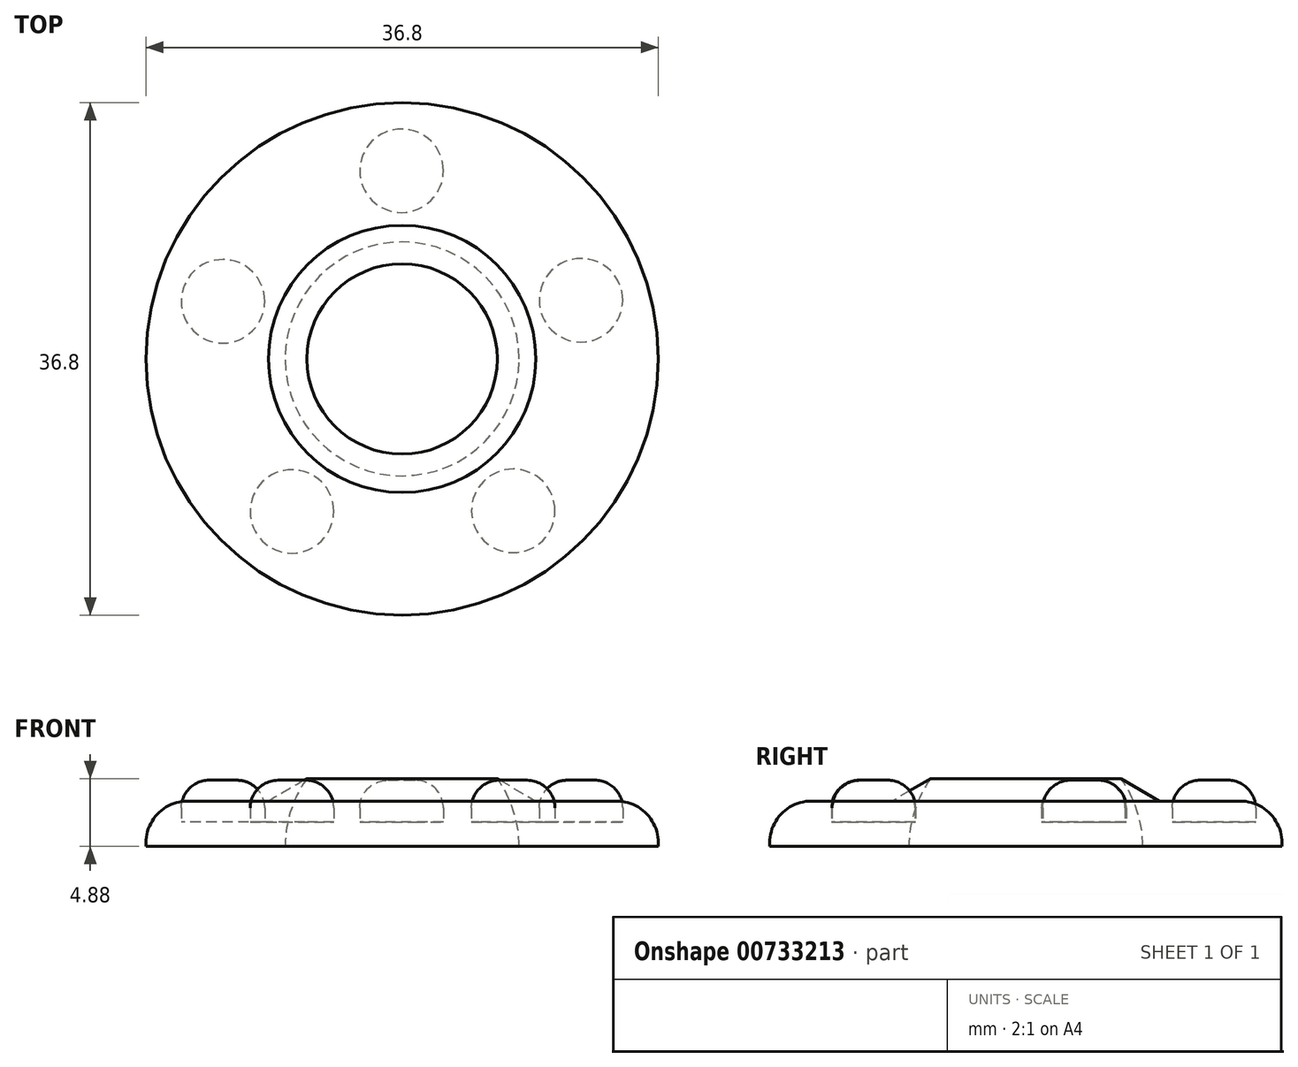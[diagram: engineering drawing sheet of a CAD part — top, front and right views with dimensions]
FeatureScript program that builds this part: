
annotation { "Feature Type Name" : "Feature", "Feature Type Description" : "" }
export const myFeature = defineFeature(function(context is Context, id is Id, definition is map)
    precondition{}
    {
        {
            var Q0;
            Q0=qCreatedBy(makeId("Front.planeOp"),FACE);
            var sketch = newSketch(context, id + "F0", { "sketchPlane" : qUnion([Q0])});
            skLineSegment(sketch, "E0", {"start": v(0, 7.97) * mm, "end": v(0, 8.4) * mm});
            skArc(sketch, "E1", {"start": v(-6.84, 4.88) * mm, "mid": v(-8, 2.56) * mm, "end": v(-8.4, 0) * mm});
            skLineSegment(sketch, "E2", {"start": v(-18.4, 0) * mm, "end": v(-18.4, 4.3) * mm});
            skLineSegment(sketch, "E3", {"start": v(-21.26, 3.26) * mm, "end": v(-9.6, 3.26) * mm});
            skLineSegment(sketch, "E4.trimOffspring", {"start": v(-8.4, 0) * mm, "end": v(-18.4, 0) * mm});
            skCircle(sketch, "E5", {"center": v(0, 0) * mm, "radius": 8 * mm});
            skLineSegment(sketch, "E6", {"start": v(0, 0) * mm, "end": v(-8, 0) * mm});
            skLineSegment(sketch, "E7", {"start": v(-9.6, 3.26) * mm, "end": v(-6.84, 4.88) * mm});
            skSolve(sketch);
        }
        {
            var Q0;
            Q0=makeQuery(id+"F0.imprint","IMPRINT",FACE,{"disambiguationData":[TD([[makeQuery(id+"F0.imprint","IMPRINT",EDGE,{"derivedFrom":sQuery(id+"F0.wireOp",EDGE,"E1")}),-1.0]])]});
            var Q1;
            Q1=sQuery(id+"F0.wireOp",EDGE,"E0");
            revolve(context, id + "F1", {"surfaceOperationType" : NewSurfaceOperationType.NEW, "entities" : qUnion([Q0]), "axis" : qUnion([Q1]), "revolveType" : RevolveType.FULL});
        }
        {
            var Q0;
            Q0=makeQuery(id+"F1.opRevolve","SWEPT_FACE",FACE,{"disambiguationData":[OSD([sQuery(id+"F0.wireOp",EDGE,"E3")])]});
            var sketch = newSketch(context, id + "F2", { "sketchPlane" : qUnion([Q0])});
            skCircle(sketch, "E8", {"center": v(-12.87, 4.14) * mm, "radius": 3 * mm});
            skSolve(sketch);
        }
        {
            var Q0;
            Q0=makeQuery(id+"F2.imprint","IMPRINT",FACE,{"disambiguationData":[TD([[makeQuery(id+"F2.imprint","IMPRINT",EDGE,{"derivedFrom":sQuery(id+"F2.wireOp",EDGE,"E8")}),1.0]])]});
            extrude(context, id + "F3", {"entities" : qUnion([Q0]), "endBound" : BoundingType.SYMMETRIC, "depth" : 3 * mm, "offsetDistance" : 25 * mm});
        }
        {
            var Q0;
            Q0=makeQuery(id+"F3.opExtrude","CAP_EDGE",EDGE,{"disambiguationData":[OSD([sQuery(id+"F2.wireOp",EDGE,"E8")])],"isStart":false});
            fillet(context, id + "F4", {"entities" : qUnion([Q0]), "radius" : 2 * mm, "tangentPropagation" : true, "allowEdgeOverflow" : false});
        }
        {
            var Q0;
            Q0=makeQuery(id+"F3.opExtrude","SWEPT_BODY",BODY,{"disambiguationData":[OSD([sQuery(id+"F2.wireOp",EDGE,"E8")])]});
            var Q1;
            Q1=makeQuery(id+"F1.opRevolve","SWEPT_EDGE",EDGE,{"disambiguationData":[OSD([sQuery(id+"F0.wireOp",EDGE,"E1"),sQuery(id+"F0.wireOp",EDGE,"E7")])]});
            circularPattern(context, id + "F5", {"entities" : qUnion([Q0]), "axis" : qUnion([Q1]), "angle" : 360 * degree, "instanceCount" : 5, "equalSpace" : true});
        }
        {
            var Q0;
            Q0=makeQuery(id+"F1.opRevolve","SWEPT_EDGE",EDGE,{"disambiguationData":[OSD([sQuery(id+"F0.wireOp",EDGE,"E2"),sQuery(id+"F0.wireOp",EDGE,"E3")])]});
            fillet(context, id + "F6", {"entities" : qUnion([Q0]), "radius" : 3 * mm, "tangentPropagation" : true, "allowEdgeOverflow" : false});
        }
    });
